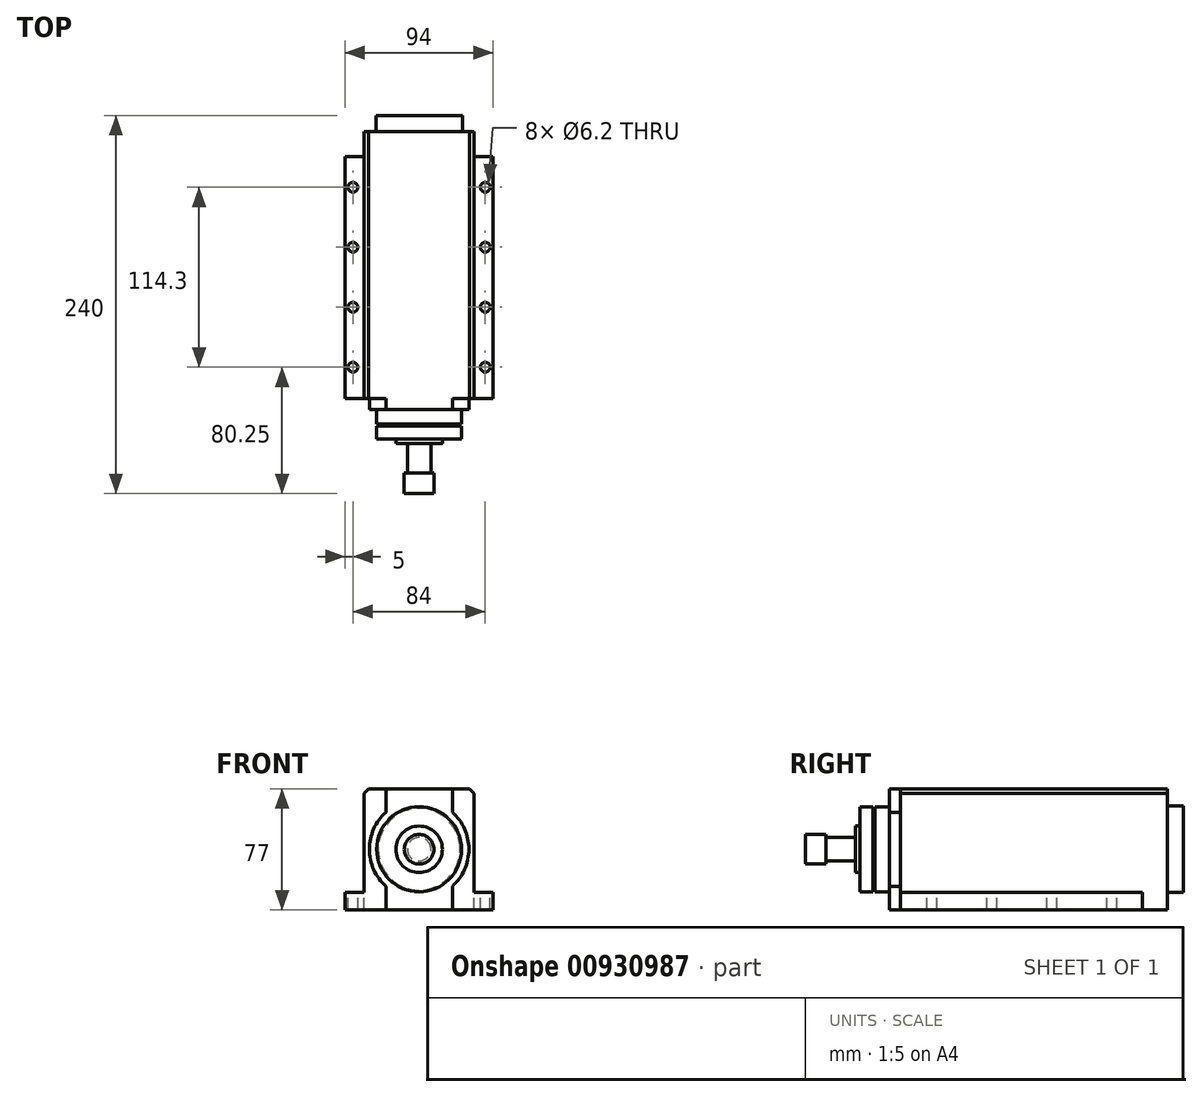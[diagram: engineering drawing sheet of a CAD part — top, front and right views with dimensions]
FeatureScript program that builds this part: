
annotation { "Feature Type Name" : "Feature", "Feature Type Description" : "" }
export const myFeature = defineFeature(function(context is Context, id is Id, definition is map)
    precondition{}
    {
        {
            var Q0;
            Q0=qCreatedBy(makeId("Front.planeOp"),FACE);
            var sketch = newSketch(context, id + "F0", { "sketchPlane" : qUnion([Q0])});
            skLineSegment(sketch, "E0", {"start": v(0, 0) * mm, "end": v(94, 0) * mm});
            skLineSegment(sketch, "E1", {"start": v(94, 0) * mm, "end": v(94, 11) * mm});
            skLineSegment(sketch, "E2", {"start": v(94, 11) * mm, "end": v(82, 11) * mm});
            skLineSegment(sketch, "E3", {"start": v(82, 11) * mm, "end": v(82, 77) * mm});
            skLineSegment(sketch, "E4", {"start": v(82, 77) * mm, "end": v(12, 77) * mm});
            skLineSegment(sketch, "E5", {"start": v(12, 77) * mm, "end": v(12, 11) * mm});
            skLineSegment(sketch, "E6", {"start": v(12, 11) * mm, "end": v(0, 11) * mm});
            skLineSegment(sketch, "E7", {"start": v(0, 11) * mm, "end": v(0, 0) * mm});
            skSolve(sketch);
        }
        {
            var Q0;
            Q0 = qSketchRegion(id + "F0", true);
            extrude(context, id + "F1", {"entities" : qUnion([Q0]), "depth" : 153.75 * mm, "offsetDistance" : 25 * mm});
        }
        {
            var Q0;
            Q0=makeQuery(id+"F1.opExtrude","SWEPT_EDGE",EDGE,{"disambiguationData":[OSD([sQuery(id+"F0.wireOp",EDGE,"E4"),sQuery(id+"F0.wireOp",EDGE,"E5")])]});
            var Q1;
            Q1=makeQuery(id+"F1.opExtrude","SWEPT_EDGE",EDGE,{"disambiguationData":[OSD([sQuery(id+"F0.wireOp",EDGE,"E3"),sQuery(id+"F0.wireOp",EDGE,"E4")])]});
            chamfer(context, id + "F2", {"entities" : qUnion([Q0, Q1]), "width" : 3 * mm, "tangentPropagation" : true});
        }
        {
            var Q0;
            Q0=makeQuery(id+"F1.opExtrude","SWEPT_FACE",FACE,{"disambiguationData":[OSD([sQuery(id+"F0.wireOp",EDGE,"E2")])]});
            var sketch = newSketch(context, id + "F3", { "sketchPlane" : qUnion([Q0])});
            skCircle(sketch, "E8", {"center": v(89, -133.75) * mm, "radius": 3.1 * mm});
            skCircle(sketch, "E9", {"center": v(89, -95.65) * mm, "radius": 3.1 * mm});
            skCircle(sketch, "E10", {"center": v(89, -57.55) * mm, "radius": 3.1 * mm});
            skCircle(sketch, "E11", {"center": v(89, -19.45) * mm, "radius": 3.1 * mm});
            skLineSegment(sketch, "E12", {"start": v(47, -133.75) * mm, "end": v(47, -19.45) * mm, "construction": true});
            skCircle(sketch, "E13.MirrorC", {"center": v(5, -19.45) * mm, "radius": 3.1 * mm});
            skCircle(sketch, "E14.MirrorC", {"center": v(5, -57.55) * mm, "radius": 3.1 * mm});
            skCircle(sketch, "E15.MirrorC", {"center": v(5, -95.65) * mm, "radius": 3.1 * mm});
            skCircle(sketch, "E16.MirrorC", {"center": v(5, -133.75) * mm, "radius": 3.1 * mm});
            skSolve(sketch);
        }
        {
            var Q0;
            Q0 = qSketchRegion(id + "F3", true);
            extrude(context, id + "F4", {"entities" : qUnion([Q0]), "operationType" : NewBodyOperationType.REMOVE, "endBound" : BoundingType.THROUGH_ALL, "oppositeDirection" : true, "depth" : 25 * mm, "offsetDistance" : 25 * mm});
        }
        {
            var Q0;
            Q0=makeQuery(id+"F1.opExtrude","CAP_FACE",FACE,{"disambiguationData":[OSD([sQuery(id+"F0.wireOp",EDGE,"E0"),sQuery(id+"F0.wireOp",EDGE,"E1"),sQuery(id+"F0.wireOp",EDGE,"E2"),sQuery(id+"F0.wireOp",EDGE,"E3"),sQuery(id+"F0.wireOp",EDGE,"E4"),sQuery(id+"F0.wireOp",EDGE,"E5"),sQuery(id+"F0.wireOp",EDGE,"E6"),sQuery(id+"F0.wireOp",EDGE,"E7")])],"isStart":false});
            var sketch = newSketch(context, id + "F5", { "sketchPlane" : qUnion([Q0])});
            skArc(sketch, "E17", {"start": v(25.93, 62.06) * mm, "mid": v(15.39, 38.5) * mm, "end": v(25.93, 14.94) * mm});
            skPoint(sketch, "E17.centerSnap0", {"position": v(47, 77) * mm});
            skLineSegment(sketch, "E18.bottom", {"start": v(25.93, 62.06) * mm, "end": v(68.07, 62.06) * mm, "construction": true});
            skLineSegment(sketch, "E18.top", {"start": v(25.93, 77) * mm, "end": v(68.07, 77) * mm});
            skLineSegment(sketch, "E18.left", {"start": v(25.93, 62.06) * mm, "end": v(25.93, 77) * mm});
            skLineSegment(sketch, "E18.right", {"start": v(68.07, 62.06) * mm, "end": v(68.07, 77) * mm});
            skLineSegment(sketch, "E19", {"start": v(47, 38.5) * mm, "end": v(82, 38.5) * mm, "construction": true});
            skLineSegment(sketch, "E20.MirrorCS", {"start": v(68.07, 14.94) * mm, "end": v(68.07, 0) * mm});
            skLineSegment(sketch, "E21.MirrorCS", {"start": v(25.93, 0) * mm, "end": v(68.07, 0) * mm});
            skLineSegment(sketch, "E22.MirrorCS", {"start": v(25.93, 14.94) * mm, "end": v(25.93, 0) * mm});
            skArc(sketch, "E23.trimOffspring", {"start": v(68.07, 14.94) * mm, "mid": v(78.6, 38.5) * mm, "end": v(68.07, 62.06) * mm});
            skSolve(sketch);
        }
        {
            var Q0;
            Q0 = qSketchRegion(id + "F5", true);
            extrude(context, id + "F6", {"entities" : qUnion([Q0]), "operationType" : NewBodyOperationType.ADD, "depth" : 7 * mm, "offsetDistance" : 25 * mm});
        }
        {
            var Q0;
            Q0=makeQuery(id+"F6.opExtrude","CAP_FACE",FACE,{"disambiguationData":[OSD([sQuery(id+"F5.wireOp",EDGE,"E17"),sQuery(id+"F5.wireOp",EDGE,"E18.top"),sQuery(id+"F5.wireOp",EDGE,"E18.left"),sQuery(id+"F5.wireOp",EDGE,"E18.right"),sQuery(id+"F5.wireOp",EDGE,"E20.MirrorCS"),sQuery(id+"F5.wireOp",EDGE,"E21.MirrorCS"),sQuery(id+"F5.wireOp",EDGE,"E22.MirrorCS"),sQuery(id+"F5.wireOp",EDGE,"E23.trimOffspring")])],"isStart":false});
            var sketch = newSketch(context, id + "F7", { "sketchPlane" : qUnion([Q0])});
            skCircle(sketch, "E24", {"center": v(47, 38.5) * mm, "radius": 27 * mm});
            skSolve(sketch);
        }
        {
            var Q0;
            Q0 = qSketchRegion(id + "F7", true);
            extrude(context, id + "F8", {"entities" : qUnion([Q0]), "operationType" : NewBodyOperationType.ADD, "depth" : 18.67 * mm, "offsetDistance" : 25 * mm});
        }
        {
            var Q0;
            Q0=makeQuery(id+"F8.opExtrude","CAP_FACE",FACE,{"disambiguationData":[OSD([sQuery(id+"F7.wireOp",EDGE,"E24")])],"isStart":false});
            var sketch = newSketch(context, id + "F9", { "sketchPlane" : qUnion([Q0])});
            skCircle(sketch, "E25", {"center": v(47, 38.5) * mm, "radius": 14.75 * mm});
            skSolve(sketch);
        }
        {
            var Q0;
            Q0=makeQuery(id+"F9.imprint","IMPRINT",FACE,{"disambiguationData":[TD([[makeQuery(id+"F9.imprint","IMPRINT",EDGE,{"derivedFrom":sQuery(id+"F9.wireOp",EDGE,"E25")}),1.0]])]});
            extrude(context, id + "F10", {"entities" : qUnion([Q0]), "operationType" : NewBodyOperationType.ADD, "depth" : 3 * mm, "offsetDistance" : 25 * mm});
        }
        {
            var Q0;
            Q0=qCreatedBy(makeId("Right.planeOp"),FACE);
            cPlane(context, id + "F11", {"entities" : qUnion([Q0]), "cplaneType" : CPlaneType.OFFSET, "offset" : (94 / 2) * mm, "width" : 150 * mm, "height" : 150 * mm});
        }
        {
            var Q0;
            Q0=qCreatedBy(id+"F11.planeOp",FACE);
            var sketch = newSketch(context, id + "F12", { "sketchPlane" : qUnion([Q0])});
            skLineSegment(sketch, "E26.bottom", {"start": v(-171, 65.5) * mm, "end": v(-170, 65.5) * mm});
            skLineSegment(sketch, "E26.top", {"start": v(-171, 64.5) * mm, "end": v(-170, 64.5) * mm});
            skLineSegment(sketch, "E26.left", {"start": v(-171, 65.5) * mm, "end": v(-171, 64.5) * mm});
            skLineSegment(sketch, "E26.right", {"start": v(-170, 65.5) * mm, "end": v(-170, 64.5) * mm});
            skSolve(sketch);
        }
        {
            var Q0;
            Q0 = qSketchRegion(id + "F12", true);
            var Q1;
            Q1=makeQuery(id+"F8.opExtrude","SWEPT_FACE",FACE,{"disambiguationData":[OSD([sQuery(id+"F7.wireOp",EDGE,"E24")])]});
            revolve(context, id + "F13", {"operationType" : NewBodyOperationType.REMOVE, "surfaceOperationType" : NewSurfaceOperationType.NEW, "entities" : qUnion([Q0]), "axis" : qUnion([Q1]), "revolveType" : RevolveType.FULL, "oppositeDirection" : true});
        }
        {
            var Q0;
            Q0=makeQuery(id+"F10.opExtrude","CAP_FACE",FACE,{"disambiguationData":[OSD([sQuery(id+"F9.wireOp",EDGE,"E25")])],"isStart":false});
            var sketch = newSketch(context, id + "F14", { "sketchPlane" : qUnion([Q0])});
            skCircle(sketch, "E27", {"center": v(47, 38.5) * mm, "radius": 7.5 * mm});
            skSolve(sketch);
        }
        {
            var Q0;
            Q0=makeQuery(id+"F14.imprint","IMPRINT",FACE,{"disambiguationData":[TD([[makeQuery(id+"F14.imprint","IMPRINT",EDGE,{"derivedFrom":sQuery(id+"F14.wireOp",EDGE,"E27")}),1.0]])]});
            extrude(context, id + "F15", {"entities" : qUnion([Q0]), "operationType" : NewBodyOperationType.ADD, "depth" : 18.5 * mm, "offsetDistance" : 25 * mm});
        }
        {
            var Q0;
            Q0=makeQuery(id+"F15.opExtrude","CAP_FACE",FACE,{"disambiguationData":[OSD([sQuery(id+"F14.wireOp",EDGE,"E27")])],"isStart":false});
            var sketch = newSketch(context, id + "F16", { "sketchPlane" : qUnion([Q0])});
            skCircle(sketch, "E28", {"center": v(47, 38.5) * mm, "radius": 9.43 * mm});
            skSolve(sketch);
        }
        {
            var Q0;
            Q0=makeQuery(id+"F16.imprint","IMPRINT",FACE,{"disambiguationData":[TD([[makeQuery(id+"F16.imprint","IMPRINT",EDGE,{"derivedFrom":sQuery(id+"F16.wireOp",EDGE,"E28")}),1.0]])]});
            var Q1;
            Q1=makeQuery(id+"F16.imprint","IMPRINT",FACE,{"disambiguationData":[TD([[makeQuery(id+"F16.imprint","IMPRINT",EDGE,{"derivedFrom":makeQuery(id+"F15.opExtrude","CAP_EDGE",EDGE,{"disambiguationData":[OSD([sQuery(id+"F14.wireOp",EDGE,"E27")])],"isStart":false})}),1.0]])]});
            extrude(context, id + "F17", {"entities" : qUnion([Q0, Q1]), "operationType" : NewBodyOperationType.ADD, "depth" : 13.08 * mm, "offsetDistance" : 25 * mm});
        }
        {
            var Q0;
            Q0=makeQuery(id+"F1.opExtrude","CAP_FACE",FACE,{"disambiguationData":[OSD([sQuery(id+"F0.wireOp",EDGE,"E0"),sQuery(id+"F0.wireOp",EDGE,"E1"),sQuery(id+"F0.wireOp",EDGE,"E2"),sQuery(id+"F0.wireOp",EDGE,"E3"),sQuery(id+"F0.wireOp",EDGE,"E4"),sQuery(id+"F0.wireOp",EDGE,"E5"),sQuery(id+"F0.wireOp",EDGE,"E6"),sQuery(id+"F0.wireOp",EDGE,"E7")])],"isStart":true});
            var sketch = newSketch(context, id + "F18", { "sketchPlane" : qUnion([Q0])});
            skLineSegment(sketch, "E29", {"start": v(-82, 74) * mm, "end": v(-82, 0) * mm});
            skLineSegment(sketch, "E30", {"start": v(-82, 0) * mm, "end": v(-12, 0) * mm});
            skLineSegment(sketch, "E31", {"start": v(-12, 0) * mm, "end": v(-12, 74) * mm});
            skLineSegment(sketch, "E32", {"start": v(-12, 74) * mm, "end": v(-15, 77) * mm});
            skLineSegment(sketch, "E33", {"start": v(-15, 77) * mm, "end": v(-79, 77) * mm});
            skLineSegment(sketch, "E34", {"start": v(-79, 77) * mm, "end": v(-82, 74) * mm});
            skSolve(sketch);
        }
        {
            var Q0;
            Q0 = qSketchRegion(id + "F18", true);
            extrude(context, id + "F19", {"entities" : qUnion([Q0]), "operationType" : NewBodyOperationType.ADD, "depth" : 16 * mm, "offsetDistance" : 25 * mm});
        }
        {
            var Q0;
            Q0=makeQuery(id+"F19.opExtrude","CAP_FACE",FACE,{"disambiguationData":[OSD([sQuery(id+"F18.wireOp",EDGE,"E29"),sQuery(id+"F18.wireOp",EDGE,"E30"),sQuery(id+"F18.wireOp",EDGE,"E31"),sQuery(id+"F18.wireOp",EDGE,"E32"),sQuery(id+"F18.wireOp",EDGE,"E33"),sQuery(id+"F18.wireOp",EDGE,"E34")])],"isStart":false});
            var sketch = newSketch(context, id + "F20", { "sketchPlane" : qUnion([Q0])});
            skCircle(sketch, "E35", {"center": v(-47, 38.5) * mm, "radius": 27.5 * mm});
            skPoint(sketch, "E35.centerSnap0", {"position": v(-47, 77) * mm});
            skSolve(sketch);
        }
        {
            var Q0;
            Q0=makeQuery(id+"F20.imprint","IMPRINT",FACE,{"disambiguationData":[TD([[makeQuery(id+"F20.imprint","IMPRINT",EDGE,{"derivedFrom":sQuery(id+"F20.wireOp",EDGE,"E35")}),1.0]])]});
            var Q1;
            Q1=sQuery(id+"F20.wireOp",EDGE,"E35");
            extrude(context, id + "F21", {"entities" : qUnion([Q0]), "operationType" : NewBodyOperationType.ADD, "surfaceEntities" : qUnion([Q1]), "depth" : 10 * mm, "offsetDistance" : 25 * mm});
        }
        {
            var Q0;
            Q0=makeQuery(id+"F19.opExtrude","CAP_FACE",FACE,{"disambiguationData":[OSD([sQuery(id+"F18.wireOp",EDGE,"E29"),sQuery(id+"F18.wireOp",EDGE,"E30"),sQuery(id+"F18.wireOp",EDGE,"E31"),sQuery(id+"F18.wireOp",EDGE,"E32"),sQuery(id+"F18.wireOp",EDGE,"E33"),sQuery(id+"F18.wireOp",EDGE,"E34")])],"isStart":false});
            var sketch = newSketch(context, id + "F22", { "sketchPlane" : qUnion([Q0])});
            skLineSegment(sketch, "E36", {"start": v(-82, 0) * mm, "end": v(-12, 0) * mm});
            skLineSegment(sketch, "E37", {"start": v(-12, 0) * mm, "end": v(-12, 74) * mm});
            skLineSegment(sketch, "E38", {"start": v(-12, 74) * mm, "end": v(-15, 77) * mm});
            skLineSegment(sketch, "E39", {"start": v(-15, 77) * mm, "end": v(-79, 77) * mm});
            skLineSegment(sketch, "E40", {"start": v(-79, 77) * mm, "end": v(-82, 74) * mm});
            skLineSegment(sketch, "E41", {"start": v(-82, 74) * mm, "end": v(-82, 0) * mm});
            skSolve(sketch);
        }
        {
            var Q1;
            Q1 = qSketchRegion(id + "F22", true);
            var Q2;
            Q2=makeQuery(id+"F21.opExtrude","CAP_FACE",FACE,{"disambiguationData":[OSD([sQuery(id+"F20.wireOp",EDGE,"E35")])],"isStart":false});
            var Q3;
            Q3 = qConstructionFilter(qBodyType(qCreatedBy(id + "F22" ,EDGE), BodyType.WIRE), ConstructionObject.NO);
            var Q4;
            Q4=makeQuery(id+"F21.opExtrude","CAP_EDGE",EDGE,{"disambiguationData":[OSD([sQuery(id+"F20.wireOp",EDGE,"E35")])],"isStart":false});
            loft(context, id + "F23", {"bodyType" : ToolBodyType.SURFACE, "operationType" : NewBodyOperationType.ADD, "startCondition" : LoftEndDerivativeType.NORMAL_TO_PROFILE, "startMagnitude" : 1, "sheetProfilesArray" : [{ "sheetProfileEntities" : qUnion([Q1]) }, { "sheetProfileEntities" : qUnion([Q2]) }], "wireProfilesArray" : [{ "wireProfileEntities" : qUnion([Q3]) }, { "wireProfileEntities" : qUnion([Q4]) }]});
        }
    });
